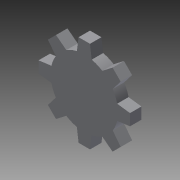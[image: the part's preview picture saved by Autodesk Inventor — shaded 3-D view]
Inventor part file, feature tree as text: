
AUTODESK INVENTOR PART (.ipt)
format: ipt  version: 2013 (Build 170138000, 138)  size: 108,032 bytes
history: native  units: in
note: dims shown in document units (in); Inventor stores cm internally (conversion verified against a paired STEP export)
features: extrude x1, sketch x1
ambient origin geometry x8: Origin, YZ Plane, XZ Plane, XY Plane, X Axis, Y Axis, Z Axis, Center Point
bodies: Solid1 (feature_tree)
feature tree (2):
  extrude  "Extrusion1"  Depth=0.071in
  sketch  "Sketch1"  dims[d0=0.0625in d2=0.071in d3=3.1496in d5=360.0deg d7=120.0deg d8=0.0625in d9=0.0in]
